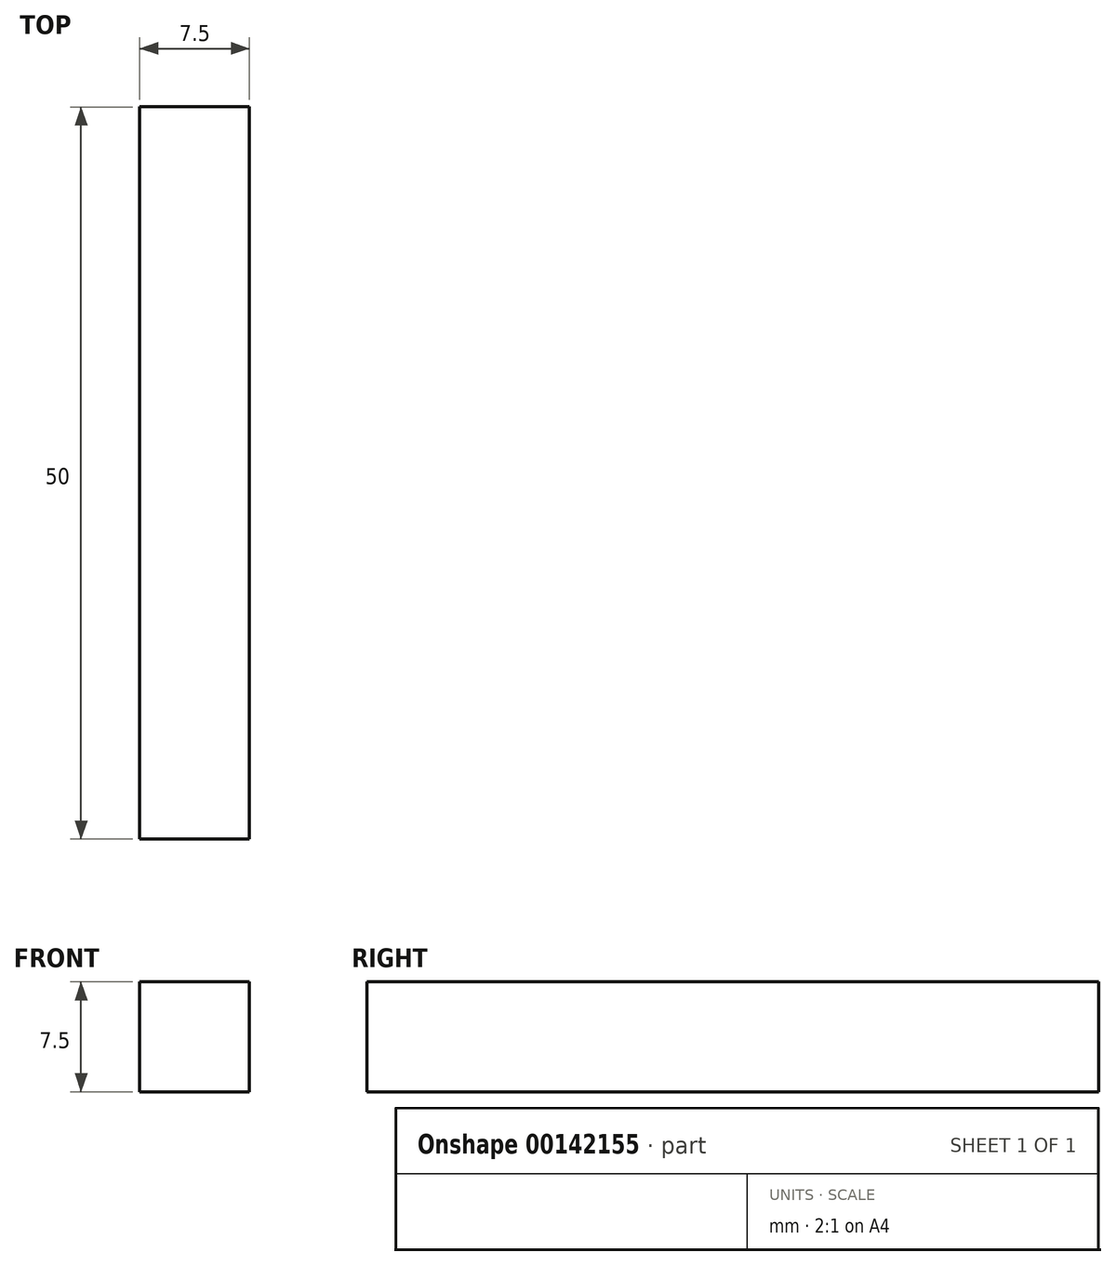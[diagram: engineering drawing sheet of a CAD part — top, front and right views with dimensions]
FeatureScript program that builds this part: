
annotation { "Feature Type Name" : "Feature", "Feature Type Description" : "" }
export const myFeature = defineFeature(function(context is Context, id is Id, definition is map)
    precondition{}
    {
        {
            var Q0;
            Q0=qCreatedBy(makeId("Top.planeOp"),FACE);
            var sketch = newSketch(context, id + "F0", { "sketchPlane" : qUnion([Q0])});
            skLineSegment(sketch, "E0.bottom", {"start": v(-0.28, 20.7) * mm, "end": v(7.22, 20.7) * mm});
            skLineSegment(sketch, "E0.top", {"start": v(-0.28, -29.3) * mm, "end": v(7.22, -29.3) * mm});
            skLineSegment(sketch, "E0.left", {"start": v(-0.28, 20.7) * mm, "end": v(-0.28, -29.3) * mm});
            skLineSegment(sketch, "E0.right", {"start": v(7.22, 20.7) * mm, "end": v(7.22, -29.3) * mm});
            skSolve(sketch);
        }
        {
            var Q0;
            Q0 = qSketchRegion(id + "F0", true);
            extrude(context, id + "F1", {"entities" : qUnion([Q0]), "depth" : 7.5 * mm});
        }
    });
